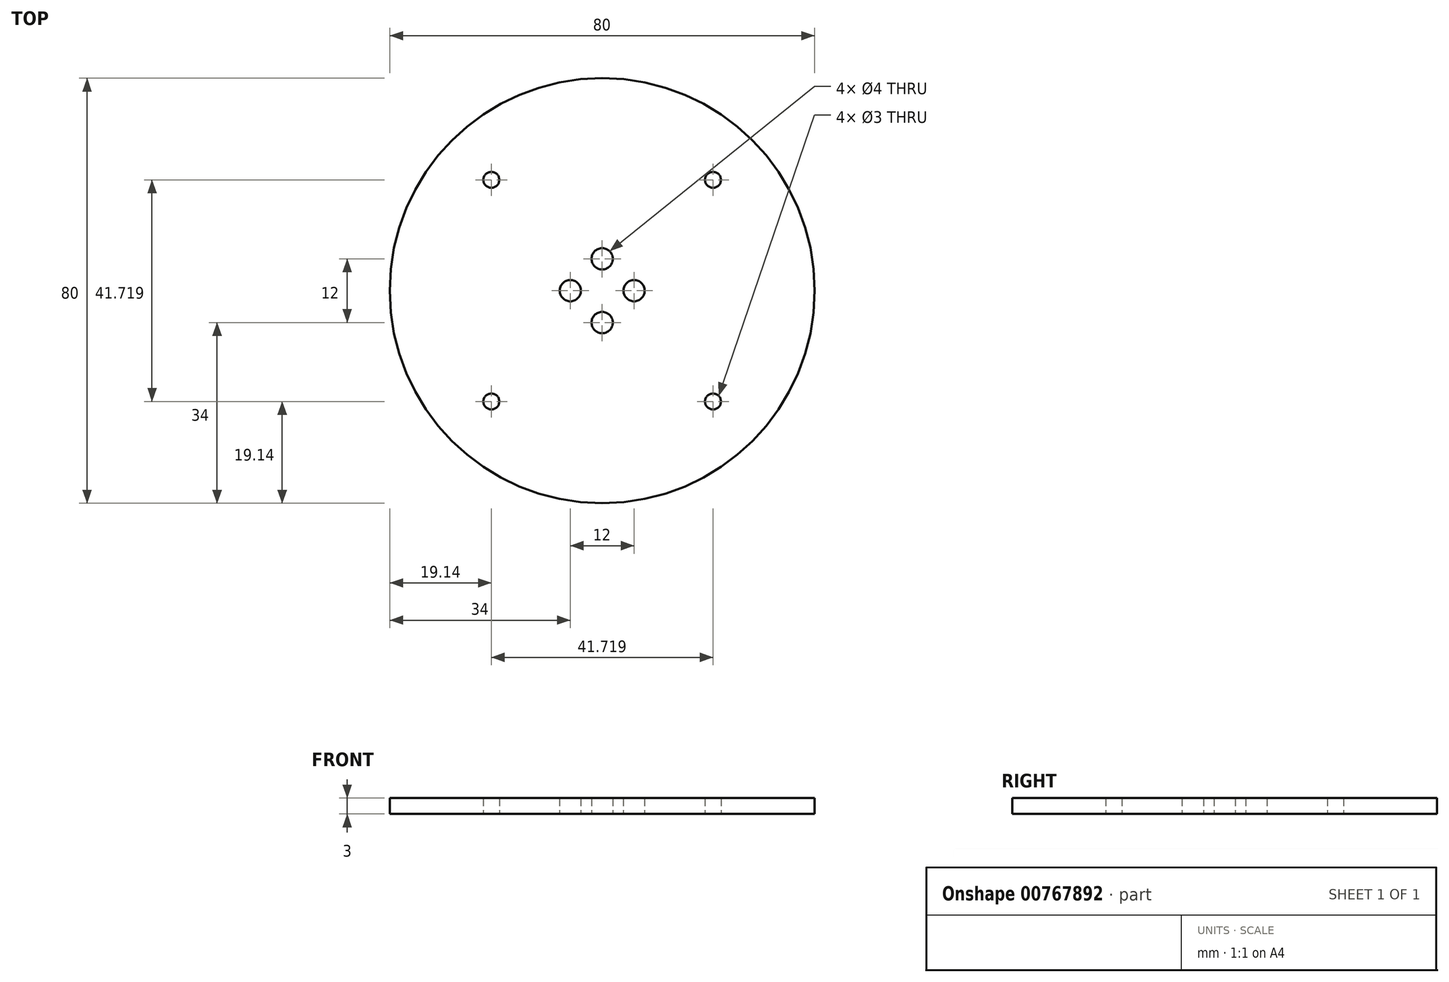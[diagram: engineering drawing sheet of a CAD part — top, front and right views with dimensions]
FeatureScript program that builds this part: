
annotation { "Feature Type Name" : "Feature", "Feature Type Description" : "" }
export const myFeature = defineFeature(function(context is Context, id is Id, definition is map)
    precondition{}
    {
        {
            var Q0;
            Q0=qCreatedBy(makeId("Top.planeOp"),FACE);
            var sketch = newSketch(context, id + "F0", { "sketchPlane" : qUnion([Q0])});
            skCircle(sketch, "E0", {"center": v(0, 0) * mm, "radius": 40 * mm});
            skLineSegment(sketch, "E1", {"start": v(0, 40) * mm, "end": v(0, -40) * mm, "construction": true});
            skLineSegment(sketch, "E2", {"start": v(-40, 0) * mm, "end": v(40, 0) * mm, "construction": true});
            skCircle(sketch, "E3", {"center": v(6, 0) * mm, "radius": 2 * mm});
            skCircle(sketch, "E4.1.0", {"center": v(0, 6) * mm, "radius": 2 * mm});
            skCircle(sketch, "E4.2.0", {"center": v(-6, 0) * mm, "radius": 2 * mm});
            skCircle(sketch, "E4.3.0", {"center": v(0, -6) * mm, "radius": 2 * mm});
            skCircle(sketch, "E5", {"center": v(0, 0) * mm, "radius": 29.5 * mm, "construction": true});
            skLineSegment(sketch, "E6", {"start": v(0, 0) * mm, "end": v(36.8, 36.8) * mm, "construction": true});
            skCircle(sketch, "E7", {"center": v(20.86, 20.86) * mm, "radius": 1.5 * mm});
            skCircle(sketch, "E8.1.0", {"center": v(-20.86, 20.86) * mm, "radius": 1.5 * mm});
            skCircle(sketch, "E8.2.0", {"center": v(-20.86, -20.86) * mm, "radius": 1.5 * mm});
            skCircle(sketch, "E8.3.0", {"center": v(20.86, -20.86) * mm, "radius": 1.5 * mm});
            skSolve(sketch);
        }
        {
            var Q0;
            Q0 = qSketchRegion(id + "F0", true);
            extrude(context, id + "F1", {"entities" : qUnion([Q0]), "depth" : 3 * mm, "offsetDistance" : 25 * mm});
        }
    });
